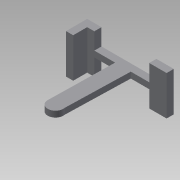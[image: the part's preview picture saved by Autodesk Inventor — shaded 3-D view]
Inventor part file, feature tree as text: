
AUTODESK INVENTOR PART (.ipt)
format: ipt  version: 2015 SP1 (Build 190203100, 203)  size: 266,240 bytes
history: native  units: mm
features: extrude x18, sketch x16, plane x2, projected_geometry x2
ambient origin geometry x8: Origin, YZ Plane, XZ Plane, XY Plane, X Axis, Y Axis, Z Axis, Center Point
bodies: Solid1 (feature_tree)
feature tree (38):
  plane  "Work Plane5"
  sketch  "Sketch4"  dims[d34=15.0mm d36=2.0mm]
  extrude  "Extrusion7"  Depth=2.0mm
  extrude  "Extrusion8"  Depth=2.5mm TaperAngle=0.0deg
  plane  "Work Plane4"
  extrude  "Extrusion9"  Depth=2.0mm
  extrude  "Extrusion10"  Depth=2.0mm
  extrude  "Extrusion11"  Depth=4.0mm TaperAngle=0.0deg
  extrude  "Extrusion12"  Depth=2.0mm TaperAngle=0.0deg
  extrude  "Extrusion13"  Depth=17.0mm TaperAngle=0.0deg
  extrude  "Extrusion14"  Depth=4.0mm TaperAngle=0.0deg
  extrude  "Extrusion15"  Depth=4.0mm TaperAngle=0.0deg
  extrude  "Extrusion16"  Depth=17.0mm TaperAngle=0.0deg
  extrude  "Extrusion18"  Depth=3.0mm
  extrude  "Extrusion19"  Depth=3.0mm TaperAngle=0.0deg
  extrude  "Extrusion20"  Depth=2.0mm
  extrude  "Extrusion21"  Depth=2.0mm TaperAngle=0.0deg
  sketch  "Sketch19"  dims[d78=2.0mm d79=2.0mm d80=0.0mm]
  extrude  "Extrusion22"  Depth=3.0mm TaperAngle=0.0deg
  extrude  "Extrusion23"  Depth=3.0mm
  extrude  "Extrusion24"  Depth=3.0mm TaperAngle=0.0deg
  extrude  "Extrusion25"  [1 undecoded]
  sketch  "Sketch5"  dims[d37=2.5mm d38=0.0mm d39=17.0mm d40=0.0mm]
  sketch  "Sketch6"  dims[d41=17.0mm d42=0.0mm d43=2.0mm]
  sketch  "Sketch7"  dims[d44=2.0mm d45=2.0mm]
  sketch  "Sketch8"  dims[d46=2.0mm d47=4.0mm d48=0.0mm]
  sketch  "Sketch9"  dims[d49=5.0mm d50=2.0mm d51=0.0mm]
  sketch  "Sketch10"  dims[d52=2.0mm d53=17.0mm d54=0.0mm]
  sketch  "Sketch12"  dims[d55=2.0mm d56=0.0mm d57=4.0mm d58=0.0mm]
  sketch  "Sketch13"  dims[d59=1.0mm d60=4.0mm d61=0.0mm]
  sketch  "Sketch15"  dims[d62=1.0mm d63=17.0mm d64=0.0mm]
  sketch  "Sketch16"  dims[d68=3.0mm d69=0.0mm d70=3.0mm]
  sketch  "Sketch17"  dims[d71=3.0mm d72=0.0mm d73=2.0mm d74=0.0mm]
  projected_geometry  "Projected Loop2"
  sketch  "Sketch18"  dims[d75=2.0mm d76=0.0mm d77=2.0mm]
  projected_geometry  "Projected Loop3"
  sketch  "Sketch20"  dims[d81=3.0mm d82=0.0mm d83=3.0mm d84=0.0mm]
  sketch  "Sketch21"  dims[d85=0.25mm d86=0.25mm d87=3.0mm d88=0.0mm]
note: 1 required parameter value undecoded (feature->parameter linkage not recoverable at this tier; creation-order binding heuristic only, values carry confidence <= 0.55)
